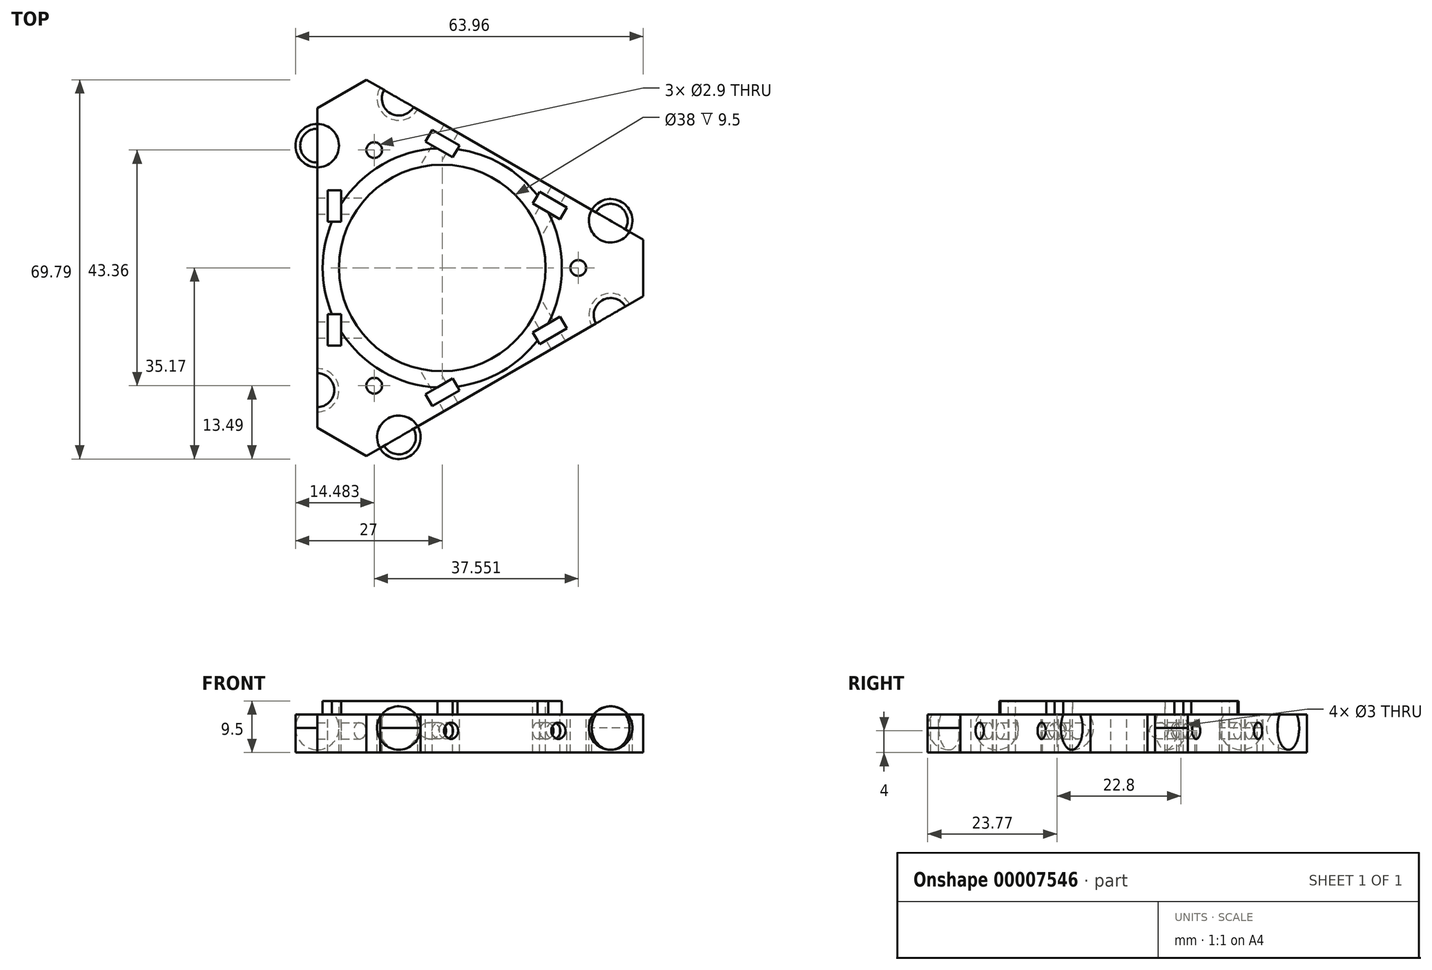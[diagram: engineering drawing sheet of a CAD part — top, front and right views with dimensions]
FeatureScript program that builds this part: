
annotation { "Feature Type Name" : "Feature", "Feature Type Description" : "" }
export const myFeature = defineFeature(function(context is Context, id is Id, definition is map)
    precondition{}
    {
        {
            var Q0;
            Q0=qCreatedBy(makeId("Top.planeOp"),FACE);
            var sketch = newSketch(context, id + "F0", { "sketchPlane" : qUnion([Q0])});
            skCircle(sketch, "E0", {"center": v(0, 0) * mm, "radius": 19 * mm});
            skLineSegment(sketch, "E1", {"start": v(0, 0) * mm, "end": v(-23, 0) * mm, "construction": true});
            skLineSegment(sketch, "E2", {"start": v(-23, 0) * mm, "end": v(-23, 22.5) * mm, "construction": true});
            skCircle(sketch, "E3", {"center": v(-23, 22.5) * mm, "radius": 4 * mm});
            skCircle(sketch, "E4", {"center": v(-23, -22.5) * mm, "radius": 4 * mm});
            skLineSegment(sketch, "E5", {"start": v(-23, 39.84) * mm, "end": v(-23, -39.84) * mm});
            skLineSegment(sketch, "E6", {"start": v(-23, -39.84) * mm, "end": v(0, 0) * mm});
            skLineSegment(sketch, "E7", {"start": v(0, 0) * mm, "end": v(-23, 39.84) * mm});
            skLineSegment(sketch, "E8", {"start": v(-23, 29.4) * mm, "end": v(-18.48, 32) * mm});
            skLineSegment(sketch, "E9", {"start": v(-23, -29.4) * mm, "end": v(-18.48, -32) * mm});
            skLineSegment(sketch, "E10.1.0", {"start": v(-13.96, -34.62) * mm, "end": v(-18.48, -32) * mm});
            skCircle(sketch, "E10.1.1", {"center": v(-7.99, -31.17) * mm, "radius": 4 * mm});
            skLineSegment(sketch, "E10.1.2", {"start": v(-23, -39.84) * mm, "end": v(46, 0) * mm});
            skCircle(sketch, "E10.1.3", {"center": v(30.99, -8.67) * mm, "radius": 4 * mm});
            skLineSegment(sketch, "E10.1.4", {"start": v(36.96, -5.22) * mm, "end": v(36.96, 0) * mm});
            skLineSegment(sketch, "E10.2.0", {"start": v(36.96, 5.22) * mm, "end": v(36.96, 0) * mm});
            skCircle(sketch, "E10.2.1", {"center": v(30.99, 8.67) * mm, "radius": 4 * mm});
            skLineSegment(sketch, "E10.2.2", {"start": v(46, 0) * mm, "end": v(-23, 39.84) * mm});
            skCircle(sketch, "E10.2.3", {"center": v(-7.99, 31.17) * mm, "radius": 4 * mm});
            skLineSegment(sketch, "E10.2.4", {"start": v(-13.96, 34.62) * mm, "end": v(-18.48, 32) * mm});
            skCircle(sketch, "E11", {"center": v(0, 0) * mm, "radius": 22 * mm});
            skCircle(sketch, "E12", {"center": v(-12.52, 21.68) * mm, "radius": 1.45 * mm});
            skCircle(sketch, "E13.1.0", {"center": v(-12.52, -21.68) * mm, "radius": 1.45 * mm});
            skCircle(sketch, "E13.2.0", {"center": v(25.03, 0) * mm, "radius": 1.45 * mm});
            skLineSegment(sketch, "E14", {"start": v(-23, 0) * mm, "end": v(-23, 11.4) * mm});
            skLineSegment(sketch, "E15.rect.bottom", {"start": v(-21.1, 8.5) * mm, "end": v(-18.6, 8.5) * mm});
            skLineSegment(sketch, "E15.rect.top", {"start": v(-21.1, 14.3) * mm, "end": v(-18.6, 14.3) * mm});
            skLineSegment(sketch, "E15.rect.left", {"start": v(-21.1, 8.5) * mm, "end": v(-21.1, 14.3) * mm});
            skLineSegment(sketch, "E15.rect.right", {"start": v(-18.6, 8.5) * mm, "end": v(-18.6, 14.3) * mm});
            skPoint(sketch, "E15.rect.middle", {"position": v(-19.85, 11.4) * mm});
            skLineSegment(sketch, "E16.0.MirrorCS", {"start": v(-21.1, -8.5) * mm, "end": v(-21.1, -14.3) * mm});
            skLineSegment(sketch, "E17.0.MirrorCS", {"start": v(-21.1, -14.3) * mm, "end": v(-18.6, -14.3) * mm});
            skLineSegment(sketch, "E18.0.MirrorCS", {"start": v(-18.6, -8.5) * mm, "end": v(-18.6, -14.3) * mm});
            skLineSegment(sketch, "E19.0.MirrorCS", {"start": v(-21.1, -8.5) * mm, "end": v(-18.6, -8.5) * mm});
            skLineSegment(sketch, "E20.1.0", {"start": v(3.19, -22.52) * mm, "end": v(-1.83, -25.42) * mm});
            skLineSegment(sketch, "E20.1.1", {"start": v(-1.83, -25.42) * mm, "end": v(-3.08, -23.26) * mm});
            skLineSegment(sketch, "E20.1.2", {"start": v(1.94, -20.36) * mm, "end": v(-3.08, -23.26) * mm});
            skLineSegment(sketch, "E20.1.3", {"start": v(3.19, -22.52) * mm, "end": v(1.94, -20.36) * mm});
            skLineSegment(sketch, "E20.1.4", {"start": v(17.91, -14.02) * mm, "end": v(16.66, -11.86) * mm});
            skLineSegment(sketch, "E20.1.5", {"start": v(16.66, -11.86) * mm, "end": v(21.68, -8.96) * mm});
            skLineSegment(sketch, "E20.1.6", {"start": v(17.91, -14.02) * mm, "end": v(22.93, -11.12) * mm});
            skLineSegment(sketch, "E20.1.7", {"start": v(22.93, -11.12) * mm, "end": v(21.68, -8.96) * mm});
            skLineSegment(sketch, "E20.2.0", {"start": v(17.91, 14.02) * mm, "end": v(22.93, 11.12) * mm});
            skLineSegment(sketch, "E20.2.1", {"start": v(22.93, 11.12) * mm, "end": v(21.68, 8.96) * mm});
            skLineSegment(sketch, "E20.2.2", {"start": v(16.66, 11.86) * mm, "end": v(21.68, 8.96) * mm});
            skLineSegment(sketch, "E20.2.3", {"start": v(17.91, 14.02) * mm, "end": v(16.66, 11.86) * mm});
            skLineSegment(sketch, "E20.2.4", {"start": v(3.19, 22.52) * mm, "end": v(1.94, 20.36) * mm});
            skLineSegment(sketch, "E20.2.5", {"start": v(1.94, 20.36) * mm, "end": v(-3.08, 23.26) * mm});
            skLineSegment(sketch, "E20.2.6", {"start": v(3.19, 22.52) * mm, "end": v(-1.83, 25.42) * mm});
            skLineSegment(sketch, "E20.2.7", {"start": v(-1.83, 25.42) * mm, "end": v(-3.08, 23.26) * mm});
            skSolve(sketch);
        }
        {
            var Q0;
            {var subQ5=sQuery(id+"F0.wireOp",EDGE,"E8");Q0=makeQuery(id+"F0.imprint","IMPRINT",FACE,{"disambiguationData":[TD([[makeQuery(id+"F0.imprint","IMPRINT",EDGE,{"derivedFrom":subQ5}),-1.0]])]});}
            var Q1;
            {var subQ28=sQuery(id+"F0.wireOp",EDGE,"E10.1.0");Q1=makeQuery(id+"F0.imprint","IMPRINT",FACE,{"disambiguationData":[TD([[makeQuery(id+"F0.imprint","IMPRINT",EDGE,{"derivedFrom":subQ28}),-1.0]])]});}
            var Q2;
            {var subQ3=sQuery(id+"F0.wireOp",EDGE,"E6");var subQ5=sQuery(id+"F0.wireOp",EDGE,"E0");var subQ7=makeQuery(id+"F0.imprint","INTERSECT",VERTEX,{"derivedFrom":[subQ5,subQ3]});Q2=makeQuery(id+"F0.imprint","IMPRINT",FACE,{"disambiguationData":[TD([[makeQuery(id+"F0.imprint","IMPRINT",EDGE,{"disambiguationData":[TD([[subQ7,1.0]])],"derivedFrom":subQ5}),-1.0]])]});}
            var Q3;
            {var subQ3=sQuery(id+"F0.wireOp",EDGE,"E6");var subQ5=sQuery(id+"F0.wireOp",EDGE,"E0");var subQ7=makeQuery(id+"F0.imprint","INTERSECT",VERTEX,{"derivedFrom":[subQ5,subQ3]});Q3=makeQuery(id+"F0.imprint","IMPRINT",FACE,{"disambiguationData":[TD([[makeQuery(id+"F0.imprint","IMPRINT",EDGE,{"disambiguationData":[TD([[subQ7,-1.0]])],"derivedFrom":subQ5}),-1.0]])]});}
            var Q4;
            {var subQ0=sQuery(id+"F0.wireOp",EDGE,"E5");var subQ1=sQuery(id+"F0.wireOp",EDGE,"E3");var subQ3=makeQuery(id+"F0.imprint","INTERSECT",VERTEX,{"disambiguationData":[OD(0.0)],"derivedFrom":[subQ1,subQ0]});Q4=makeQuery(id+"F0.imprint","IMPRINT",FACE,{"disambiguationData":[TD([[makeQuery(id+"F0.imprint","IMPRINT",EDGE,{"disambiguationData":[TD([[subQ3,1.0]])],"derivedFrom":subQ1}),1.0]])]});}
            var Q5;
            {var subQ0=sQuery(id+"F0.wireOp",EDGE,"E10.2.3");var subQ1=sQuery(id+"F0.wireOp",EDGE,"E10.2.2");var subQ3=makeQuery(id+"F0.imprint","INTERSECT",VERTEX,{"disambiguationData":[OD(0.0)],"derivedFrom":[subQ1,subQ0]});Q5=makeQuery(id+"F0.imprint","IMPRINT",FACE,{"disambiguationData":[TD([[makeQuery(id+"F0.imprint","IMPRINT",EDGE,{"disambiguationData":[TD([[subQ3,-1.0]])],"derivedFrom":subQ1}),1.0]])]});}
            var Q6;
            {var subQ0=sQuery(id+"F0.wireOp",EDGE,"E10.2.2");var subQ1=sQuery(id+"F0.wireOp",EDGE,"E10.2.1");var subQ3=makeQuery(id+"F0.imprint","INTERSECT",VERTEX,{"disambiguationData":[OD(0.0)],"derivedFrom":[subQ1,subQ0]});Q6=makeQuery(id+"F0.imprint","IMPRINT",FACE,{"disambiguationData":[TD([[makeQuery(id+"F0.imprint","IMPRINT",EDGE,{"disambiguationData":[TD([[subQ3,1.0]])],"derivedFrom":subQ1}),1.0]])]});}
            var Q7;
            {var subQ0=sQuery(id+"F0.wireOp",EDGE,"E10.1.3");var subQ1=sQuery(id+"F0.wireOp",EDGE,"E10.1.2");var subQ3=makeQuery(id+"F0.imprint","INTERSECT",VERTEX,{"disambiguationData":[OD(0.0)],"derivedFrom":[subQ1,subQ0]});Q7=makeQuery(id+"F0.imprint","IMPRINT",FACE,{"disambiguationData":[TD([[makeQuery(id+"F0.imprint","IMPRINT",EDGE,{"disambiguationData":[TD([[subQ3,-1.0]])],"derivedFrom":subQ1}),1.0]])]});}
            var Q8;
            {var subQ0=sQuery(id+"F0.wireOp",EDGE,"E10.1.2");var subQ1=sQuery(id+"F0.wireOp",EDGE,"E10.1.1");var subQ3=makeQuery(id+"F0.imprint","INTERSECT",VERTEX,{"disambiguationData":[OD(0.0)],"derivedFrom":[subQ1,subQ0]});Q8=makeQuery(id+"F0.imprint","IMPRINT",FACE,{"disambiguationData":[TD([[makeQuery(id+"F0.imprint","IMPRINT",EDGE,{"disambiguationData":[TD([[subQ3,1.0]])],"derivedFrom":subQ1}),1.0]])]});}
            var Q9;
            {var subQ0=sQuery(id+"F0.wireOp",EDGE,"E5");var subQ1=sQuery(id+"F0.wireOp",EDGE,"E4");var subQ3=makeQuery(id+"F0.imprint","INTERSECT",VERTEX,{"disambiguationData":[OD(0.0)],"derivedFrom":[subQ1,subQ0]});Q9=makeQuery(id+"F0.imprint","IMPRINT",FACE,{"disambiguationData":[TD([[makeQuery(id+"F0.imprint","IMPRINT",EDGE,{"disambiguationData":[TD([[subQ3,1.0]])],"derivedFrom":subQ1}),1.0]])]});}
            extrude(context, id + "F1", {"entities" : qUnion([Q0, Q1, Q2, Q3, Q4, Q5, Q6, Q7, Q8, Q9]), "oppositeDirection" : true, "depth" : 4.5 * mm});
        }
        {
            var Q0;
            {var subQ5=sQuery(id+"F0.wireOp",EDGE,"E8");Q0=makeQuery(id+"F0.imprint","IMPRINT",FACE,{"disambiguationData":[TD([[makeQuery(id+"F0.imprint","IMPRINT",EDGE,{"derivedFrom":subQ5}),-1.0]])]});}
            var Q1;
            {var subQ0=sQuery(id+"F0.wireOp",EDGE,"E5");var subQ1=sQuery(id+"F0.wireOp",EDGE,"E3");var subQ3=makeQuery(id+"F0.imprint","INTERSECT",VERTEX,{"disambiguationData":[OD(0.0)],"derivedFrom":[subQ1,subQ0]});Q1=makeQuery(id+"F0.imprint","IMPRINT",FACE,{"disambiguationData":[TD([[makeQuery(id+"F0.imprint","IMPRINT",EDGE,{"disambiguationData":[TD([[subQ3,1.0]])],"derivedFrom":subQ1}),1.0]])]});}
            var Q2;
            {var subQ0=sQuery(id+"F0.wireOp",EDGE,"E10.2.3");var subQ1=sQuery(id+"F0.wireOp",EDGE,"E10.2.2");var subQ3=makeQuery(id+"F0.imprint","INTERSECT",VERTEX,{"disambiguationData":[OD(0.0)],"derivedFrom":[subQ1,subQ0]});Q2=makeQuery(id+"F0.imprint","IMPRINT",FACE,{"disambiguationData":[TD([[makeQuery(id+"F0.imprint","IMPRINT",EDGE,{"disambiguationData":[TD([[subQ3,-1.0]])],"derivedFrom":subQ1}),1.0]])]});}
            var Q3;
            {var subQ28=sQuery(id+"F0.wireOp",EDGE,"E10.1.0");Q3=makeQuery(id+"F0.imprint","IMPRINT",FACE,{"disambiguationData":[TD([[makeQuery(id+"F0.imprint","IMPRINT",EDGE,{"derivedFrom":subQ28}),-1.0]])]});}
            var Q4;
            {var subQ0=sQuery(id+"F0.wireOp",EDGE,"E10.2.2");var subQ1=sQuery(id+"F0.wireOp",EDGE,"E10.2.1");var subQ3=makeQuery(id+"F0.imprint","INTERSECT",VERTEX,{"disambiguationData":[OD(0.0)],"derivedFrom":[subQ1,subQ0]});Q4=makeQuery(id+"F0.imprint","IMPRINT",FACE,{"disambiguationData":[TD([[makeQuery(id+"F0.imprint","IMPRINT",EDGE,{"disambiguationData":[TD([[subQ3,1.0]])],"derivedFrom":subQ1}),1.0]])]});}
            var Q5;
            {var subQ0=sQuery(id+"F0.wireOp",EDGE,"E10.1.3");var subQ1=sQuery(id+"F0.wireOp",EDGE,"E10.1.2");var subQ3=makeQuery(id+"F0.imprint","INTERSECT",VERTEX,{"disambiguationData":[OD(0.0)],"derivedFrom":[subQ1,subQ0]});Q5=makeQuery(id+"F0.imprint","IMPRINT",FACE,{"disambiguationData":[TD([[makeQuery(id+"F0.imprint","IMPRINT",EDGE,{"disambiguationData":[TD([[subQ3,-1.0]])],"derivedFrom":subQ1}),1.0]])]});}
            var Q6;
            {var subQ0=sQuery(id+"F0.wireOp",EDGE,"E5");var subQ1=sQuery(id+"F0.wireOp",EDGE,"E4");var subQ3=makeQuery(id+"F0.imprint","INTERSECT",VERTEX,{"disambiguationData":[OD(0.0)],"derivedFrom":[subQ1,subQ0]});Q6=makeQuery(id+"F0.imprint","IMPRINT",FACE,{"disambiguationData":[TD([[makeQuery(id+"F0.imprint","IMPRINT",EDGE,{"disambiguationData":[TD([[subQ3,1.0]])],"derivedFrom":subQ1}),1.0]])]});}
            var Q7;
            {var subQ0=sQuery(id+"F0.wireOp",EDGE,"E10.1.2");var subQ1=sQuery(id+"F0.wireOp",EDGE,"E10.1.1");var subQ3=makeQuery(id+"F0.imprint","INTERSECT",VERTEX,{"disambiguationData":[OD(0.0)],"derivedFrom":[subQ1,subQ0]});Q7=makeQuery(id+"F0.imprint","IMPRINT",FACE,{"disambiguationData":[TD([[makeQuery(id+"F0.imprint","IMPRINT",EDGE,{"disambiguationData":[TD([[subQ3,1.0]])],"derivedFrom":subQ1}),1.0]])]});}
            extrude(context, id + "F2", {"entities" : qUnion([Q0, Q1, Q2, Q3, Q4, Q5, Q6, Q7]), "operationType" : NewBodyOperationType.ADD, "depth" : 2.5 * mm});
        }
        {
            var Q0;
            {var subQ0=sQuery(id+"F0.wireOp",EDGE,"E5");var subQ1=sQuery(id+"F0.wireOp",EDGE,"E3");var subQ3=makeQuery(id+"F0.imprint","INTERSECT",VERTEX,{"disambiguationData":[OD(0.0)],"derivedFrom":[subQ1,subQ0]});Q0=makeQuery(id+"F0.imprint","IMPRINT",FACE,{"disambiguationData":[TD([[makeQuery(id+"F0.imprint","IMPRINT",EDGE,{"disambiguationData":[TD([[subQ3,-1.0]])],"derivedFrom":subQ1}),1.0]])]});}
            var Q1;
            {var subQ0=sQuery(id+"F0.wireOp",EDGE,"E5");var subQ1=sQuery(id+"F0.wireOp",EDGE,"E4");var subQ3=makeQuery(id+"F0.imprint","INTERSECT",VERTEX,{"disambiguationData":[OD(0.0)],"derivedFrom":[subQ1,subQ0]});Q1=makeQuery(id+"F0.imprint","IMPRINT",FACE,{"disambiguationData":[TD([[makeQuery(id+"F0.imprint","IMPRINT",EDGE,{"disambiguationData":[TD([[subQ3,-1.0]])],"derivedFrom":subQ1}),1.0]])]});}
            var Q2;
            Q2=sQuery(id+"F0.wireOp",EDGE,"E5");
            revolve(context, id + "F3", {"operationType" : NewBodyOperationType.REMOVE, "entities" : qUnion([Q0, Q1]), "axis" : qUnion([Q2]), "revolveType" : RevolveType.FULL, "oppositeDirection" : true});
        }
        {
            var Q0;
            {var subQ0=sQuery(id+"F0.wireOp",EDGE,"E10.2.3");var subQ1=sQuery(id+"F0.wireOp",EDGE,"E10.2.2");var subQ3=makeQuery(id+"F0.imprint","INTERSECT",VERTEX,{"disambiguationData":[OD(0.0)],"derivedFrom":[subQ1,subQ0]});Q0=makeQuery(id+"F0.imprint","IMPRINT",FACE,{"disambiguationData":[TD([[makeQuery(id+"F0.imprint","IMPRINT",EDGE,{"disambiguationData":[TD([[subQ3,-1.0]])],"derivedFrom":subQ1}),-1.0]])]});}
            var Q1;
            {var subQ0=sQuery(id+"F0.wireOp",EDGE,"E10.2.2");var subQ1=sQuery(id+"F0.wireOp",EDGE,"E10.2.1");var subQ3=makeQuery(id+"F0.imprint","INTERSECT",VERTEX,{"disambiguationData":[OD(0.0)],"derivedFrom":[subQ1,subQ0]});Q1=makeQuery(id+"F0.imprint","IMPRINT",FACE,{"disambiguationData":[TD([[makeQuery(id+"F0.imprint","IMPRINT",EDGE,{"disambiguationData":[TD([[subQ3,-1.0]])],"derivedFrom":subQ1}),1.0]])]});}
            var Q2;
            Q2=sQuery(id+"F0.wireOp",EDGE,"E10.2.2");
            revolve(context, id + "F4", {"operationType" : NewBodyOperationType.REMOVE, "entities" : qUnion([Q0, Q1]), "axis" : qUnion([Q2]), "revolveType" : RevolveType.FULL, "oppositeDirection" : true});
        }
        {
            var Q0;
            {var subQ0=sQuery(id+"F0.wireOp",EDGE,"E10.1.2");var subQ1=sQuery(id+"F0.wireOp",EDGE,"E10.1.1");var subQ3=makeQuery(id+"F0.imprint","INTERSECT",VERTEX,{"disambiguationData":[OD(0.0)],"derivedFrom":[subQ1,subQ0]});Q0=makeQuery(id+"F0.imprint","IMPRINT",FACE,{"disambiguationData":[TD([[makeQuery(id+"F0.imprint","IMPRINT",EDGE,{"disambiguationData":[TD([[subQ3,-1.0]])],"derivedFrom":subQ1}),1.0]])]});}
            var Q1;
            {var subQ0=sQuery(id+"F0.wireOp",EDGE,"E10.1.3");var subQ1=sQuery(id+"F0.wireOp",EDGE,"E10.1.2");var subQ3=makeQuery(id+"F0.imprint","INTERSECT",VERTEX,{"disambiguationData":[OD(0.0)],"derivedFrom":[subQ1,subQ0]});Q1=makeQuery(id+"F0.imprint","IMPRINT",FACE,{"disambiguationData":[TD([[makeQuery(id+"F0.imprint","IMPRINT",EDGE,{"disambiguationData":[TD([[subQ3,-1.0]])],"derivedFrom":subQ1}),-1.0]])]});}
            var Q2;
            Q2=sQuery(id+"F0.wireOp",EDGE,"E10.1.2");
            revolve(context, id + "F5", {"operationType" : NewBodyOperationType.REMOVE, "entities" : qUnion([Q0, Q1]), "axis" : qUnion([Q2]), "revolveType" : RevolveType.FULL, "oppositeDirection" : true});
        }
        {
            var Q0;
            {var subQ3=sQuery(id+"F0.wireOp",EDGE,"E6");var subQ5=sQuery(id+"F0.wireOp",EDGE,"E0");var subQ7=makeQuery(id+"F0.imprint","INTERSECT",VERTEX,{"derivedFrom":[subQ5,subQ3]});Q0=makeQuery(id+"F0.imprint","IMPRINT",FACE,{"disambiguationData":[TD([[makeQuery(id+"F0.imprint","IMPRINT",EDGE,{"disambiguationData":[TD([[subQ7,-1.0]])],"derivedFrom":subQ5}),-1.0]])]});}
            var Q1;
            {var subQ3=sQuery(id+"F0.wireOp",EDGE,"E6");var subQ5=sQuery(id+"F0.wireOp",EDGE,"E0");var subQ7=makeQuery(id+"F0.imprint","INTERSECT",VERTEX,{"derivedFrom":[subQ5,subQ3]});Q1=makeQuery(id+"F0.imprint","IMPRINT",FACE,{"disambiguationData":[TD([[makeQuery(id+"F0.imprint","IMPRINT",EDGE,{"disambiguationData":[TD([[subQ7,1.0]])],"derivedFrom":subQ5}),-1.0]])]});}
            extrude(context, id + "F6", {"entities" : qUnion([Q0, Q1]), "operationType" : NewBodyOperationType.ADD, "depth" : 5 * mm});
        }
        {
            var Q0;
            {var subQ0=sQuery(id+"F0.wireOp",EDGE,"E5");var subQ1=sQuery(id+"F0.wireOp",EDGE,"E3");var subQ2=makeQuery(id+"F0.imprint","INTERSECT",VERTEX,{"disambiguationData":[OD(0.0)],"derivedFrom":[subQ1,subQ0]});var subQ3=makeQuery(id+"F0.imprint","IMPRINT",EDGE,{"disambiguationData":[TD([[makeQuery(id+"F0.imprint","INTERSECT",VERTEX,{"derivedFrom":[subQ0,sQuery(id+"F0.wireOp",EDGE,"E8")]}),-1.0]])],"derivedFrom":subQ0});var subQ4=makeQuery(id+"F0.imprint","INTERSECT",VERTEX,{"disambiguationData":[OD(1.0)],"derivedFrom":[subQ1,subQ0]});var subQ5=makeQuery(id+"F0.imprint","IMPRINT",EDGE,{"disambiguationData":[TD([[subQ2,-1.0]])],"derivedFrom":subQ0});var subQ6=makeQuery(id+"F0.imprint","IMPRINT",EDGE,{"disambiguationData":[TD([[subQ4,-1.0]])],"derivedFrom":subQ0});Q0=makeQuery(id+"F2.boolean.opBoolean","MERGE",FACE,{"derivedFrom":[makeQuery(id+"F1.opExtrude","SWEPT_FACE",FACE,{"disambiguationData":[OSD([subQ0]),TDD([subQ3,subQ5,subQ6])]}),makeQuery(id+"F2.opExtrude","SWEPT_FACE",FACE,{"disambiguationData":[OSD([subQ0]),TDD([subQ3,subQ5,subQ6])]})]});}
            var sketch = newSketch(context, id + "F7", { "sketchPlane" : qUnion([Q0])});
            skLineSegment(sketch, "E21", {"start": v(0, -0.5) * mm, "end": v(-11.4, -0.5) * mm});
            skCircle(sketch, "E22", {"center": v(-11.4, -0.5) * mm, "radius": 1.5 * mm});
            skCircle(sketch, "E23", {"center": v(11.4, -0.5) * mm, "radius": 1.5 * mm});
            skSolve(sketch);
        }
        {
            var Q0;
            Q0=makeQuery(id+"F7.imprint","IMPRINT",FACE,{"disambiguationData":[TD([[makeQuery(id+"F7.imprint","IMPRINT",EDGE,{"derivedFrom":sQuery(id+"F7.wireOp",EDGE,"E22")}),1.0]])]});
            var Q1;
            Q1=makeQuery(id+"F7.imprint","IMPRINT",FACE,{"disambiguationData":[TD([[makeQuery(id+"F7.imprint","IMPRINT",EDGE,{"derivedFrom":sQuery(id+"F7.wireOp",EDGE,"E23")}),1.0]])]});
            extrude(context, id + "F8", {"entities" : qUnion([Q0, Q1]), "endBound" : BoundingType.SYMMETRIC, "depth" : 25 * mm});
        }
        {
            var Q0;
            Q0=makeQuery(id+"F8.opExtrude","SWEPT_BODY",BODY,{"disambiguationData":[OSD([sQuery(id+"F7.wireOp",EDGE,"E22")])]});
            var Q1;
            Q1=makeQuery(id+"F8.opExtrude","SWEPT_BODY",BODY,{"disambiguationData":[OSD([sQuery(id+"F7.wireOp",EDGE,"E23")])]});
            var Q2;
            Q2=makeQuery(id+"F6.opExtrude","CAP_EDGE",EDGE,{"disambiguationData":[OSD([sQuery(id+"F0.wireOp",EDGE,"E0")])],"isStart":false});
            circularPattern(context, id + "F9", {"entities" : qUnion([Q0, Q1]), "axis" : qUnion([Q2]), "angle" : 120 * degree, "instanceCount" : 3});
        }
        {
            var Q0;
            Q0=makeQuery(id+"F9.opPattern","COPY",BODY,{"derivedFrom":makeQuery(id+"F8.opExtrude","SWEPT_BODY",BODY,{"disambiguationData":[OSD([sQuery(id+"F7.wireOp",EDGE,"E23")])]}),"instanceName":"2"});
            var Q1;
            Q1=makeQuery(id+"F9.opPattern","COPY",BODY,{"derivedFrom":makeQuery(id+"F8.opExtrude","SWEPT_BODY",BODY,{"disambiguationData":[OSD([sQuery(id+"F7.wireOp",EDGE,"E22")])]}),"instanceName":"2"});
            var Q2;
            Q2=makeQuery(id+"F9.opPattern","COPY",BODY,{"derivedFrom":makeQuery(id+"F8.opExtrude","SWEPT_BODY",BODY,{"disambiguationData":[OSD([sQuery(id+"F7.wireOp",EDGE,"E23")])]}),"instanceName":"1"});
            var Q3;
            Q3=makeQuery(id+"F9.opPattern","COPY",BODY,{"derivedFrom":makeQuery(id+"F8.opExtrude","SWEPT_BODY",BODY,{"disambiguationData":[OSD([sQuery(id+"F7.wireOp",EDGE,"E22")])]}),"instanceName":"1"});
            var Q4;
            Q4=makeQuery(id+"F8.opExtrude","SWEPT_BODY",BODY,{"disambiguationData":[OSD([sQuery(id+"F7.wireOp",EDGE,"E23")])]});
            var Q5;
            Q5=makeQuery(id+"F8.opExtrude","SWEPT_BODY",BODY,{"disambiguationData":[OSD([sQuery(id+"F7.wireOp",EDGE,"E22")])]});
            var Q6;
            Q6=makeQuery(id+"F1.opExtrude","SWEPT_BODY",BODY,{"disambiguationData":[OSD([sQuery(id+"F0.wireOp",EDGE,"E0"),sQuery(id+"F0.wireOp",EDGE,"E5"),sQuery(id+"F0.wireOp",EDGE,"E8"),sQuery(id+"F0.wireOp",EDGE,"E9"),sQuery(id+"F0.wireOp",EDGE,"E10.1.0"),sQuery(id+"F0.wireOp",EDGE,"E10.1.2"),sQuery(id+"F0.wireOp",EDGE,"E10.1.4"),sQuery(id+"F0.wireOp",EDGE,"E10.2.0"),sQuery(id+"F0.wireOp",EDGE,"E10.2.2"),sQuery(id+"F0.wireOp",EDGE,"E10.2.4"),sQuery(id+"F0.wireOp",EDGE,"E12"),sQuery(id+"F0.wireOp",EDGE,"E13.1.0"),sQuery(id+"F0.wireOp",EDGE,"E13.2.0"),sQuery(id+"F0.wireOp",EDGE,"E14"),sQuery(id+"F0.wireOp",EDGE,"E15.rect.bottom"),sQuery(id+"F0.wireOp",EDGE,"E15.rect.top"),sQuery(id+"F0.wireOp",EDGE,"E15.rect.left"),sQuery(id+"F0.wireOp",EDGE,"E15.rect.right"),sQuery(id+"F0.wireOp",EDGE,"E16.0.MirrorCS"),sQuery(id+"F0.wireOp",EDGE,"E17.0.MirrorCS"),sQuery(id+"F0.wireOp",EDGE,"E18.0.MirrorCS"),sQuery(id+"F0.wireOp",EDGE,"E19.0.MirrorCS"),sQuery(id+"F0.wireOp",EDGE,"E20.1.0"),sQuery(id+"F0.wireOp",EDGE,"E20.1.1"),sQuery(id+"F0.wireOp",EDGE,"E20.1.2"),sQuery(id+"F0.wireOp",EDGE,"E20.1.3"),sQuery(id+"F0.wireOp",EDGE,"E20.1.4"),sQuery(id+"F0.wireOp",EDGE,"E20.1.5"),sQuery(id+"F0.wireOp",EDGE,"E20.1.6"),sQuery(id+"F0.wireOp",EDGE,"E20.1.7"),sQuery(id+"F0.wireOp",EDGE,"E20.2.0"),sQuery(id+"F0.wireOp",EDGE,"E20.2.1"),sQuery(id+"F0.wireOp",EDGE,"E20.2.2"),sQuery(id+"F0.wireOp",EDGE,"E20.2.3"),sQuery(id+"F0.wireOp",EDGE,"E20.2.4"),sQuery(id+"F0.wireOp",EDGE,"E20.2.5"),sQuery(id+"F0.wireOp",EDGE,"E20.2.6"),sQuery(id+"F0.wireOp",EDGE,"E20.2.7")])]});
            booleanBodies(context, id + "F10", {"operationType" : BooleanOperationType.SUBTRACTION, "tools" : qUnion([Q0, Q1, Q2, Q3, Q4, Q5]), "targets" : qUnion([Q6])});
        }
    });
